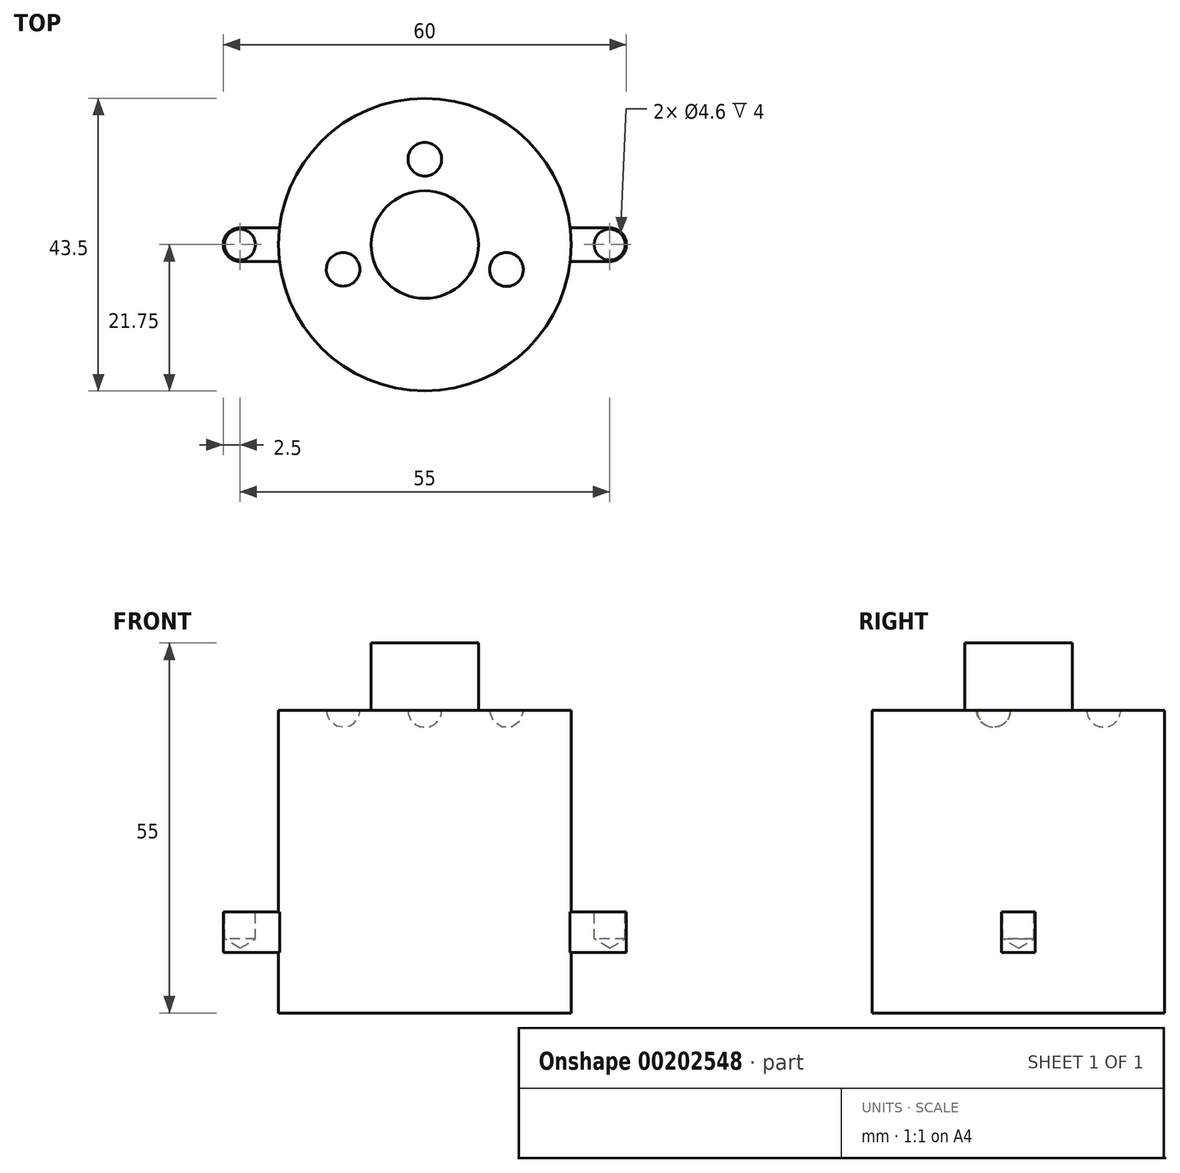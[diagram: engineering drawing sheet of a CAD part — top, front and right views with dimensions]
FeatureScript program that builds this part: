
annotation { "Feature Type Name" : "Feature", "Feature Type Description" : "" }
export const myFeature = defineFeature(function(context is Context, id is Id, definition is map)
    precondition{}
    {
        {
            var Q0;
            Q0=qCreatedBy(makeId("Right.planeOp"),FACE);
            var sketch = newSketch(context, id + "F0", { "sketchPlane" : qUnion([Q0])});
            skLineSegment(sketch, "E0.bottom", {"start": v(-21.75, -22.5) * mm, "end": v(21.75, -22.5) * mm});
            skLineSegment(sketch, "E0.top", {"start": v(-21.75, 22.5) * mm, "end": v(21.75, 22.5) * mm});
            skLineSegment(sketch, "E0.left", {"start": v(-21.75, -22.5) * mm, "end": v(-21.75, 22.5) * mm});
            skLineSegment(sketch, "E0.right", {"start": v(21.75, -22.5) * mm, "end": v(21.75, 22.5) * mm});
            skPoint(sketch, "E0.middle", {"position": v(0, 0) * mm});
            skLineSegment(sketch, "E1.bottom", {"start": v(-8, 22.5) * mm, "end": v(8, 22.5) * mm});
            skLineSegment(sketch, "E1.top", {"start": v(-8, 32.5) * mm, "end": v(8, 32.5) * mm});
            skLineSegment(sketch, "E1.left", {"start": v(-8, 22.5) * mm, "end": v(-8, 32.5) * mm});
            skLineSegment(sketch, "E1.right", {"start": v(8, 22.5) * mm, "end": v(8, 32.5) * mm});
            skPoint(sketch, "E1.middle", {"position": v(0, 27.5) * mm});
            skLineSegment(sketch, "E2", {"start": v(0, 32.5) * mm, "end": v(0, -22.5) * mm});
            skSolve(sketch);
        }
        {
            var Q0;
            {var subQ7=sQuery(id+"F0.wireOp",EDGE,"E0.left");Q0=makeQuery(id+"F0.imprint","IMPRINT",FACE,{"disambiguationData":[TD([[makeQuery(id+"F0.imprint","IMPRINT",EDGE,{"derivedFrom":subQ7}),-1.0]])]});}
            var Q1;
            {var subQ0=sQuery(id+"F0.wireOp",EDGE,"E1.left");Q1=makeQuery(id+"F0.imprint","IMPRINT",FACE,{"disambiguationData":[TD([[makeQuery(id+"F0.imprint","IMPRINT",EDGE,{"derivedFrom":subQ0}),-1.0]])]});}
            var Q2;
            Q2=sQuery(id+"F0.wireOp",EDGE,"E2");
            revolve(context, id + "F1", {"entities" : qUnion([Q0, Q1]), "axis" : qUnion([Q2]), "revolveType" : RevolveType.FULL});
        }
        {
            var Q0;
            Q0=qCreatedBy(makeId("Front.planeOp"),FACE);
            var sketch = newSketch(context, id + "F2", { "sketchPlane" : qUnion([Q0])});
            skLineSegment(sketch, "E3.bottom", {"start": v(30, -13.5) * mm, "end": v(-30, -13.5) * mm});
            skLineSegment(sketch, "E3.top", {"start": v(30, -7.5) * mm, "end": v(-30, -7.5) * mm});
            skLineSegment(sketch, "E3.left", {"start": v(30, -13.5) * mm, "end": v(30, -7.5) * mm});
            skLineSegment(sketch, "E3.right", {"start": v(-30, -13.5) * mm, "end": v(-30, -7.5) * mm});
            skPoint(sketch, "E3.middle", {"position": v(0, -10.5) * mm});
            skSolve(sketch);
        }
        {
            var Q0;
            Q0=makeQuery(id+"F2.imprint","IMPRINT",FACE,{"disambiguationData":[TD([[makeQuery(id+"F2.imprint","IMPRINT",EDGE,{"derivedFrom":sQuery(id+"F2.wireOp",EDGE,"E3.bottom")}),-1.0]])]});
            extrude(context, id + "F3", {"entities" : qUnion([Q0]), "operationType" : NewBodyOperationType.ADD, "endBound" : BoundingType.SYMMETRIC, "depth" : 5 * mm});
        }
        {
            var Q0;
            Q0=makeQuery(id+"F3.opExtrude","CAP_EDGE",EDGE,{"disambiguationData":[OSD([sQuery(id+"F2.wireOp",EDGE,"E3.left")])],"isStart":true});
            var Q1;
            Q1=makeQuery(id+"F3.opExtrude","CAP_EDGE",EDGE,{"disambiguationData":[OSD([sQuery(id+"F2.wireOp",EDGE,"E3.right")])],"isStart":true});
            var Q2;
            Q2=makeQuery(id+"F3.opExtrude","CAP_EDGE",EDGE,{"disambiguationData":[OSD([sQuery(id+"F2.wireOp",EDGE,"E3.left")])],"isStart":false});
            var Q3;
            Q3=makeQuery(id+"F3.opExtrude","CAP_EDGE",EDGE,{"disambiguationData":[OSD([sQuery(id+"F2.wireOp",EDGE,"E3.right")])],"isStart":false});
            fillet(context, id + "F4", {"entities" : qUnion([Q0, Q1, Q2, Q3]), "radius" : 2.5 * mm, "tangentPropagation" : true, "allowEdgeOverflow" : false});
        }
        {
            var Q0;
            {var subQ1=sQuery(id+"F2.wireOp",EDGE,"E3.left");var subQ2=sQuery(id+"F2.wireOp",EDGE,"E3.top");Q0=makeQuery(id+"F3.boolean.opBoolean","SPLIT",FACE,{"disambiguationData":[TD([makeQuery(id+"F3.opExtrude","SWEPT_FACE",FACE,{"disambiguationData":[OSD([subQ1])]})])],"derivedFrom":makeQuery(id+"F3.opExtrude","SWEPT_FACE",FACE,{"disambiguationData":[OSD([subQ2])]})});}
            var sketch = newSketch(context, id + "F5", { "sketchPlane" : qUnion([Q0])});
            skCircle(sketch, "E4", {"center": v(27.5, 0) * mm, "radius": 2.4 * mm});
            skCircle(sketch, "E5", {"center": v(-27.5, 0) * mm, "radius": 2.4 * mm});
            skSolve(sketch);
        }
        {
            var Q0;
            Q0=sQuery(id+"F5.wireOp",VERTEX,"E5.center");
            var Q1;
            Q1=sQuery(id+"F5.wireOp",VERTEX,"E4.center");
            var Q2;
            Q2=makeQuery(id+"F1.opRevolve","SWEPT_BODY",BODY,{"disambiguationData":[OSD([sQuery(id+"F0.wireOp",EDGE,"E0.bottom"),sQuery(id+"F0.wireOp",EDGE,"E0.top"),sQuery(id+"F0.wireOp",EDGE,"E0.left"),sQuery(id+"F0.wireOp",EDGE,"E1.top"),sQuery(id+"F0.wireOp",EDGE,"E1.left"),sQuery(id+"F0.wireOp",EDGE,"E2")])]});
            hole(context, id + "F6", {"style" : HoleStyle.SIMPLE, "endStyle" : HoleEndStyle.BLIND, "holeDiameter" : 4.6 * mm, "holeDepth" : 4 * mm, "locations" : qUnion([Q0, Q1]), "scope" : qUnion([Q2])});
        }
        {
            var Q0;
            Q0=makeQuery(id+"F1.opRevolve","SWEPT_FACE",FACE,{"disambiguationData":[OSD([sQuery(id+"F0.wireOp",EDGE,"E0.top")])]});
            var sketch = newSketch(context, id + "F7", { "sketchPlane" : qUnion([Q0])});
            skCircle(sketch, "E6", {"center": v(0, 0) * mm, "radius": 12.7 * mm, "construction": true});
            skPoint(sketch, "E7", {"position": v(0, 12.7) * mm});
            skPoint(sketch, "E8", {"position": v(12.15, -3.69) * mm});
            skPoint(sketch, "E9.MirrorP", {"position": v(-12.15, -3.69) * mm});
            skCircle(sketch, "E10", {"center": v(0, 12.7) * mm, "radius": 2.5 * mm});
            skCircle(sketch, "E11", {"center": v(12.15, -3.69) * mm, "radius": 2.5 * mm});
            skCircle(sketch, "E12.MirrorC", {"center": v(-12.15, -3.69) * mm, "radius": 2.5 * mm});
            skLineSegment(sketch, "E13", {"start": v(-14.65, -3.67) * mm, "end": v(-9.65, -3.69) * mm});
            skLineSegment(sketch, "E14", {"start": v(9.65, -3.72) * mm, "end": v(14.65, -3.69) * mm});
            skLineSegment(sketch, "E15", {"start": v(0, 15.2) * mm, "end": v(0, 10.2) * mm});
            skSolve(sketch);
        }
        {
            var Q0;
            {var subQ0=sQuery(id+"F7.wireOp",EDGE,"E15");Q0=makeQuery(id+"F7.imprint","IMPRINT",FACE,{"disambiguationData":[TD([[makeQuery(id+"F7.imprint","IMPRINT",EDGE,{"derivedFrom":subQ0}),1.0]])]});}
            var Q1;
            Q1=sQuery(id+"F7.wireOp",EDGE,"E15");
            revolve(context, id + "F8", {"operationType" : NewBodyOperationType.REMOVE, "entities" : qUnion([Q0]), "axis" : qUnion([Q1]), "revolveType" : RevolveType.FULL});
        }
        {
            var Q0;
            {var subQ0=sQuery(id+"F7.wireOp",EDGE,"E13");Q0=makeQuery(id+"F7.imprint","IMPRINT",FACE,{"disambiguationData":[TD([[makeQuery(id+"F7.imprint","IMPRINT",EDGE,{"derivedFrom":subQ0}),1.0]])]});}
            var Q1;
            Q1=sQuery(id+"F7.wireOp",EDGE,"E13");
            revolve(context, id + "F9", {"operationType" : NewBodyOperationType.REMOVE, "entities" : qUnion([Q0]), "axis" : qUnion([Q1]), "revolveType" : RevolveType.FULL});
        }
        {
            var Q0;
            {var subQ0=sQuery(id+"F7.wireOp",EDGE,"E14");Q0=makeQuery(id+"F7.imprint","IMPRINT",FACE,{"disambiguationData":[TD([[makeQuery(id+"F7.imprint","IMPRINT",EDGE,{"derivedFrom":subQ0}),1.0]])]});}
            var Q1;
            Q1=sQuery(id+"F7.wireOp",EDGE,"E14");
            revolve(context, id + "F10", {"operationType" : NewBodyOperationType.REMOVE, "entities" : qUnion([Q0]), "axis" : qUnion([Q1]), "revolveType" : RevolveType.FULL, "oppositeDirection" : true});
        }
    });
